# Revit family: Fix wallmount cabinets Legrand Linkeo with fix side panels
name_source: partatom
category: Equipement spécialisé
units: mm (PartAtom-declared; Revit-internal decimal feet)

## family parameters
Basée sur le plan de construction = Non
Cote de connecteur circulaire = Utiliser le diamètre
Couper avec des vides une fois chargée = Non
Numéro OmniClass = 23.80.30.11.17
Partagée = Oui
Point de calcul de pièce = Non
Titre OmniClass = Distribution Boards and Control Panels
Toujours verticalement = Oui
Type d'élément = Normal

## types (12) — shared parameters
Application class = Network cabinets
Avec porte frontale = Oui
Color = grey
Degree of protection IK = IK08
Degree of protection IP = IP20
Demountable = Oui
E-catalogue link = https://www.legrand.fr
Fabricant = Legrand
Function = Fix wallmount cabinets Linkeo Legrand
Material = Steel
Model = With permanent frame
Modular spacing = 482.6 mm (19 inches)
Mounting level = Front side
Number of doors = 1
RAL Number = 7016
Rack location = 40 mm  [stored 0.131234 ft]
Thickness (mm) = 1.5 mm  [stored 0.00492126 ft]
Type of profile rail = L-shaped
Type of surface = Powder coating
Type of ventilation = Passive
Usable width (mm) = 526 mm  [stored 1.72572 ft]
Width (mm) = 605 mm  [stored 1.98491 ft]
With earthing = Oui
With roof plate = Oui
With sidewall = Oui
X fixation = 400 mm  [stored 1.31234 ft]
zero-valued in all types: Elévation par défaut

## per-type parameters (varying)
| type | Depth (mm) | EAN | Height (mm) | Legrand part number | Max load capacity | Number of height units | Usable height (mm) | Y fixation |
| Fix wallmount cabinet Legrand Linkeo with fix side panels 12U W600 D450 646202.rfa | 454 mm  [stored 1.4895 ft] | 3414970967794 | 625 mm  [stored 2.05052 ft] | 646202 | 36 | 12 | 555 mm  [stored 1.82087 ft] | 419 mm |
| Fix wallmount cabinet Legrand Linkeo with fix side panels 12U W600 D600 646212.rfa | 604 mm  [stored 1.98163 ft] | 3414970967855 | 625 mm  [stored 2.05052 ft] | 646212 | 36 | 12 | 555 mm  [stored 1.82087 ft] | 419 mm |
| Fix wallmount cabinet Legrand Linkeo with fix side panels 15U W600 D450 646203.rfa | 454 mm  [stored 1.4895 ft] | 3414970967800 | 759 mm  [stored 2.49016 ft] | 646203 | 45 | 15 | 688 mm  [stored 2.25722 ft] | 552 mm  [stored 1.81102 ft] |
| Fix wallmount cabinet Legrand Linkeo with fix side panels 15U W600 D600 646213.rfa | 604 mm  [stored 1.98163 ft] | 3414970967862 | 759 mm  [stored 2.49016 ft] | 646213 | 45 | 15 | 688 mm  [stored 2.25722 ft] | 552 mm  [stored 1.81102 ft] |
| Fix wallmount cabinet Legrand Linkeo with fix side panels 18U W600 D450 646204.rfa | 454 mm  [stored 1.4895 ft] | 3414970967817 | 892 mm  [stored 2.92651 ft] | 646204 | 54 | 18 | 821 mm  [stored 2.69357 ft] | 685 mm |
| Fix wallmount cabinet Legrand Linkeo with fix side panels 18U W600 D600 646214.rfa | 604 mm  [stored 1.98163 ft] | 3414970967879 | 892 mm  [stored 2.92651 ft] | 646214 | 54 | 18 | 821 mm  [stored 2.69357 ft] | 685 mm |
| Fix wallmount cabinet Legrand Linkeo with fix side panels 21U W600 D450 646205.rfa | 454 mm  [stored 1.4895 ft] | 3414970967824 | 1025 mm  [stored 3.36286 ft] | 646205 | 63 | 21 | 955 mm  [stored 3.1332 ft] | 819 mm  [stored 2.68701 ft] |
| Fix wallmount cabinet Legrand Linkeo with fix side panels 21U W600 D600 646215.rfa | 604 mm  [stored 1.98163 ft] | 3414970967886 | 1025 mm  [stored 3.36286 ft] | 646215 | 63 | 21 | 955 mm  [stored 3.1332 ft] | 819 mm  [stored 2.68701 ft] |
| Fix wallmount cabinet Legrand Linkeo with fix side panels 6U W600 D450 646200.rfa | 454 mm  [stored 1.4895 ft] | 3414970967770 | 359 mm  [stored 1.17782 ft] | 646200 | 18 | 6 | 288 mm  [stored 0.944882 ft] | 152 mm  [stored 0.498688 ft] |
| Fix wallmount cabinet Legrand Linkeo with fix side panels 6U W600 D600 646210.rfa | 604 mm  [stored 1.98163 ft] | 3414970967831 | 359 mm  [stored 1.17782 ft] | 646210 | 18 | 6 | 288 mm  [stored 0.944882 ft] | 152 mm  [stored 0.498688 ft] |
| Fix wallmount cabinet Legrand Linkeo with fix side panels 9U W600 D450 646201.rfa | 454 mm  [stored 1.4895 ft] | 3414970967787 | 492 mm  [stored 1.61417 ft] | 646201 | 27 | 9 | 422 mm  [stored 1.38451 ft] | 286 mm |
| Fix wallmount cabinet Legrand Linkeo with fix side panels 9U W600 D600 646211.rfa | 604 mm  [stored 1.98163 ft] | 3414970967848 | 492 mm  [stored 1.61417 ft] | 646211 | 27 | 9 | 422 mm  [stored 1.38451 ft] | 286 mm |

note: column(s) folded — value = type name in every type: BIM wording

note: [stored X ft] marks values corroborated as IEEE doubles in the binary element streams (Revit-internal decimal feet)
